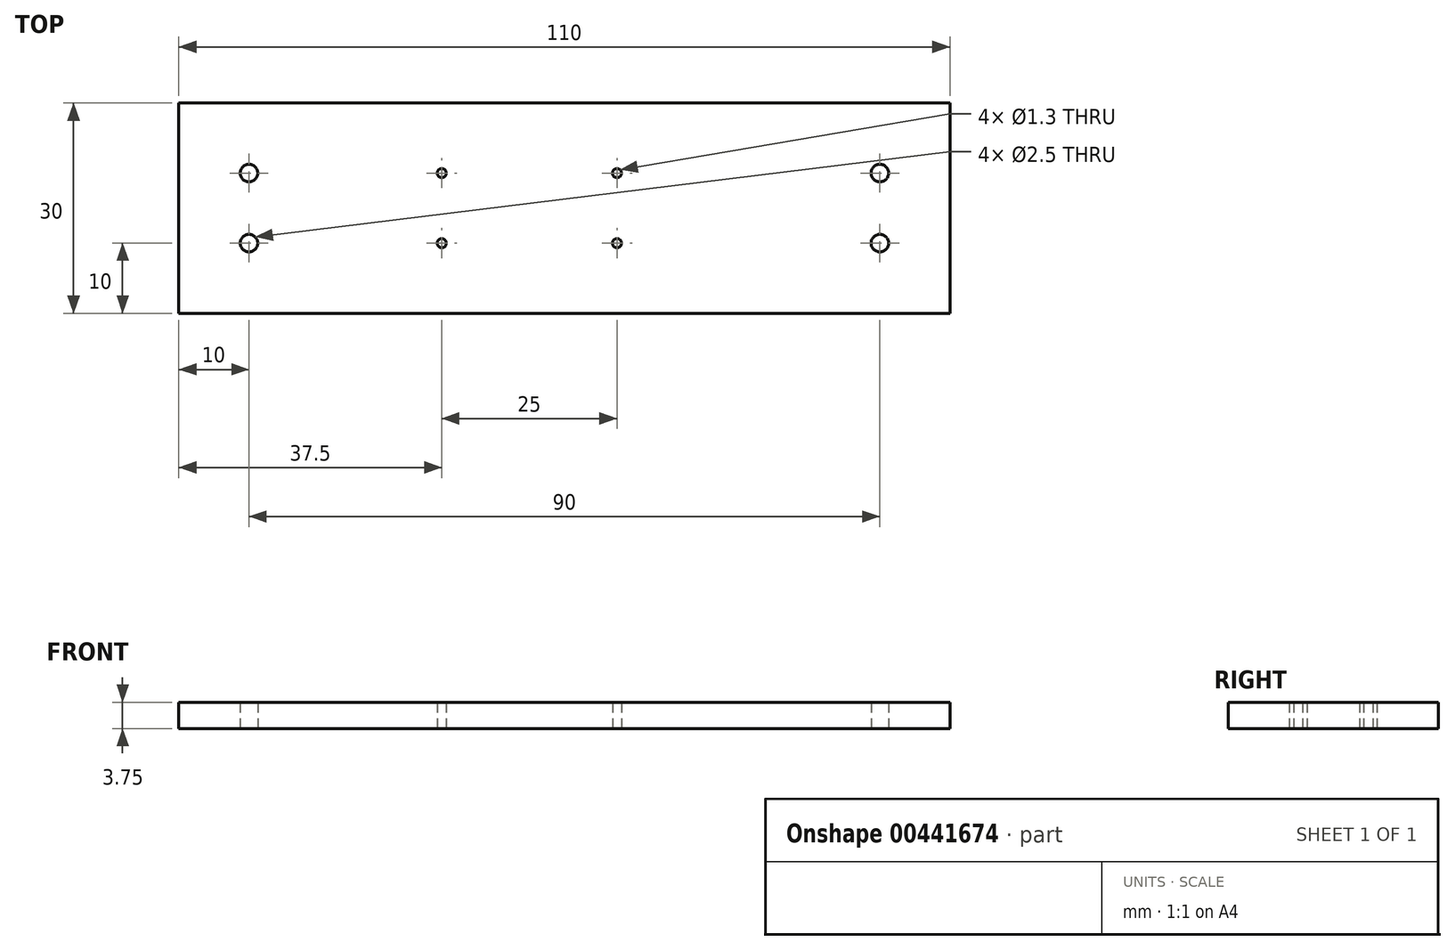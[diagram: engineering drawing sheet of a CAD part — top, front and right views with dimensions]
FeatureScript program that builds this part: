
annotation { "Feature Type Name" : "Feature", "Feature Type Description" : "" }
export const myFeature = defineFeature(function(context is Context, id is Id, definition is map)
    precondition{}
    {
        {
            var Q0;
            Q0=qCreatedBy(makeId("Top.planeOp"),FACE);
            var sketch = newSketch(context, id + "F0", { "sketchPlane" : qUnion([Q0])});
            skLineSegment(sketch, "E0.bottom", {"start": v(0, 0) * mm, "end": v(110, 0) * mm});
            skLineSegment(sketch, "E0.top", {"start": v(0, 30) * mm, "end": v(110, 30) * mm});
            skLineSegment(sketch, "E0.left", {"start": v(0, 0) * mm, "end": v(0, 30) * mm});
            skLineSegment(sketch, "E0.right", {"start": v(110, 0) * mm, "end": v(110, 30) * mm});
            skCircle(sketch, "E1", {"center": v(10, 20) * mm, "radius": 1.25 * mm});
            skCircle(sketch, "E2", {"center": v(10, 10) * mm, "radius": 1.25 * mm});
            skCircle(sketch, "E3", {"center": v(100, 20) * mm, "radius": 1.25 * mm});
            skCircle(sketch, "E4", {"center": v(100, 10) * mm, "radius": 1.25 * mm});
            skCircle(sketch, "E5", {"center": v(37.5, 20) * mm, "radius": 0.65 * mm});
            skCircle(sketch, "E6", {"center": v(37.5, 10) * mm, "radius": 0.65 * mm});
            skCircle(sketch, "E7", {"center": v(62.5, 20) * mm, "radius": 0.65 * mm});
            skCircle(sketch, "E8", {"center": v(62.5, 10) * mm, "radius": 0.65 * mm});
            skSolve(sketch);
        }
        {
            var Q0;
            Q0=makeQuery(id+"F0.imprint","IMPRINT",FACE,{"disambiguationData":[TD([[makeQuery(id+"F0.imprint","IMPRINT",EDGE,{"derivedFrom":sQuery(id+"F0.wireOp",EDGE,"E0.bottom")}),1.0]])]});
            extrude(context, id + "F1", {"entities" : qUnion([Q0]), "depth" : 3.75 * mm});
        }
    });
